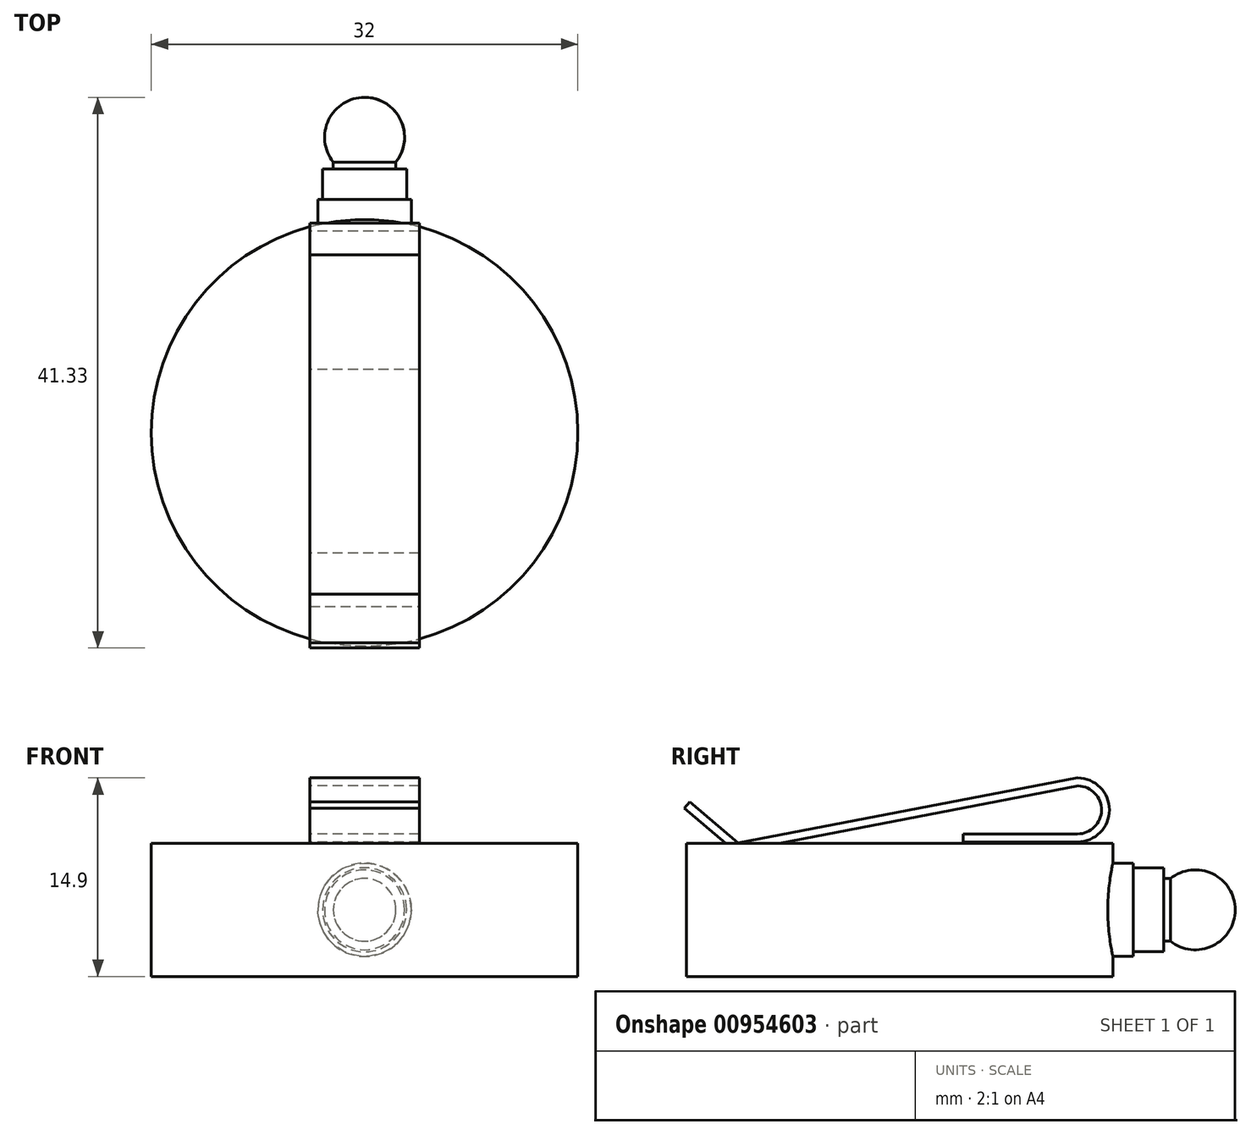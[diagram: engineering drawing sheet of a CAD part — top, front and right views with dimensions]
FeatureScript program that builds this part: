
annotation { "Feature Type Name" : "Feature", "Feature Type Description" : "" }
export const myFeature = defineFeature(function(context is Context, id is Id, definition is map)
    precondition{}
    {
        {
            var Q0;
            Q0=qCreatedBy(makeId("Top.planeOp"),FACE);
            var sketch = newSketch(context, id + "F0", { "sketchPlane" : qUnion([Q0])});
            skCircle(sketch, "E0", {"center": v(0, 0) * mm, "radius": 16 * mm});
            skSolve(sketch);
        }
        {
            var Q0;
            Q0 = qSketchRegion(id + "F0", true);
            extrude(context, id + "F1", {"entities" : qUnion([Q0]), "depth" : 10 * mm, "offsetDistance" : 25 * mm});
        }
        {
            var Q0;
            Q0=qCreatedBy(makeId("Right.planeOp"),FACE);
            var sketch = newSketch(context, id + "F2", { "sketchPlane" : qUnion([Q0])});
            skLineSegment(sketch, "E1", {"start": v(4.76, 10.1) * mm, "end": v(13.35, 10.1) * mm});
            skLineSegment(sketch, "E2", {"start": v(13.35, 10.1) * mm, "end": v(13.35, 14.9) * mm, "construction": true});
            skArc(sketch, "E3", {"start": v(13.35, 10.1) * mm, "mid": v(15.75, 12.5) * mm, "end": v(13.35, 14.9) * mm});
            skLineSegment(sketch, "E4", {"start": v(13.35, 14.9) * mm, "end": v(-12.12, 10.02) * mm});
            skLineSegment(sketch, "E5", {"start": v(-12.12, 10.02) * mm, "end": v(-15.76, 13.09) * mm});
            skLineSegment(sketch, "E6.0", {"start": v(-12.3, 9.37) * mm, "end": v(-16.15, 12.63) * mm});
            skLineSegment(sketch, "E6.1", {"start": v(13.4, 14.3) * mm, "end": v(-12.3, 9.37) * mm});
            skArc(sketch, "E6.2", {"start": v(13.35, 10.7) * mm, "mid": v(15.15, 12.47) * mm, "end": v(13.4, 14.3) * mm});
            skLineSegment(sketch, "E6.3", {"start": v(4.76, 10.7) * mm, "end": v(13.35, 10.7) * mm});
            skLineSegment(sketch, "E7", {"start": v(4.76, 10.7) * mm, "end": v(4.76, 10.1) * mm});
            skLineSegment(sketch, "E8", {"start": v(-15.76, 13.09) * mm, "end": v(-16.15, 12.63) * mm});
            skSolve(sketch);
        }
        {
            var Q0;
            Q0=makeQuery(id+"F2.imprint","IMPRINT",FACE,{"disambiguationData":[TD([[makeQuery(id+"F2.imprint","IMPRINT",EDGE,{"derivedFrom":sQuery(id+"F2.wireOp",EDGE,"E1")}),1.0]])]});
            extrude(context, id + "F3", {"entities" : qUnion([Q0]), "operationType" : NewBodyOperationType.ADD, "endBound" : BoundingType.SYMMETRIC, "depth" : 8.2 * mm, "offsetDistance" : 25 * mm});
        }
        {
            var Q0;
            Q0=qCreatedBy(makeId("Top.planeOp"),FACE);
            cPlane(context, id + "F4", {"entities" : qUnion([Q0]), "cplaneType" : CPlaneType.OFFSET, "offset" : 5 * mm, "width" : 150 * mm, "height" : 150 * mm});
        }
        {
            var Q0;
            Q0=qCreatedBy(id+"F4.planeOp",FACE);
            var sketch = newSketch(context, id + "F5", { "sketchPlane" : qUnion([Q0])});
            skLineSegment(sketch, "E9", {"start": v(0, 15.61) * mm, "end": v(0, 24.72) * mm, "construction": true});
            skLineSegment(sketch, "E10", {"start": v(0, 15.61) * mm, "end": v(-3.5, 15.61) * mm});
            skLineSegment(sketch, "E11", {"start": v(-3.5, 15.61) * mm, "end": v(-3.5, 17.51) * mm});
            skLineSegment(sketch, "E12", {"start": v(-3.5, 17.51) * mm, "end": v(0, 17.51) * mm, "construction": true});
            skLineSegment(sketch, "E13", {"start": v(-3.5, 17.51) * mm, "end": v(-3.15, 17.51) * mm});
            skLineSegment(sketch, "E14", {"start": v(-3.15, 17.51) * mm, "end": v(-3.15, 19.81) * mm});
            skLineSegment(sketch, "E15", {"start": v(-3.15, 19.81) * mm, "end": v(-2.35, 19.81) * mm});
            skLineSegment(sketch, "E16", {"start": v(-2.35, 19.81) * mm, "end": v(-2.35, 20.31) * mm});
            skArc(sketch, "E17", {"start": v(0, 25.18) * mm, "mid": v(-2.7, 23.48) * mm, "end": v(-2.35, 20.31) * mm});
            skLineSegment(sketch, "E18", {"start": v(0, 25.18) * mm, "end": v(0, 15.61) * mm});
            skSolve(sketch);
        }
        {
            var Q0;
            Q0 = qSketchRegion(id + "F5", true);
            var Q1;
            Q1=sQuery(id+"F5.wireOp",EDGE,"E18");
            revolve(context, id + "F6", {"operationType" : NewBodyOperationType.ADD, "surfaceOperationType" : NewSurfaceOperationType.NEW, "entities" : qUnion([Q0]), "axis" : qUnion([Q1]), "revolveType" : RevolveType.FULL});
        }
    });
